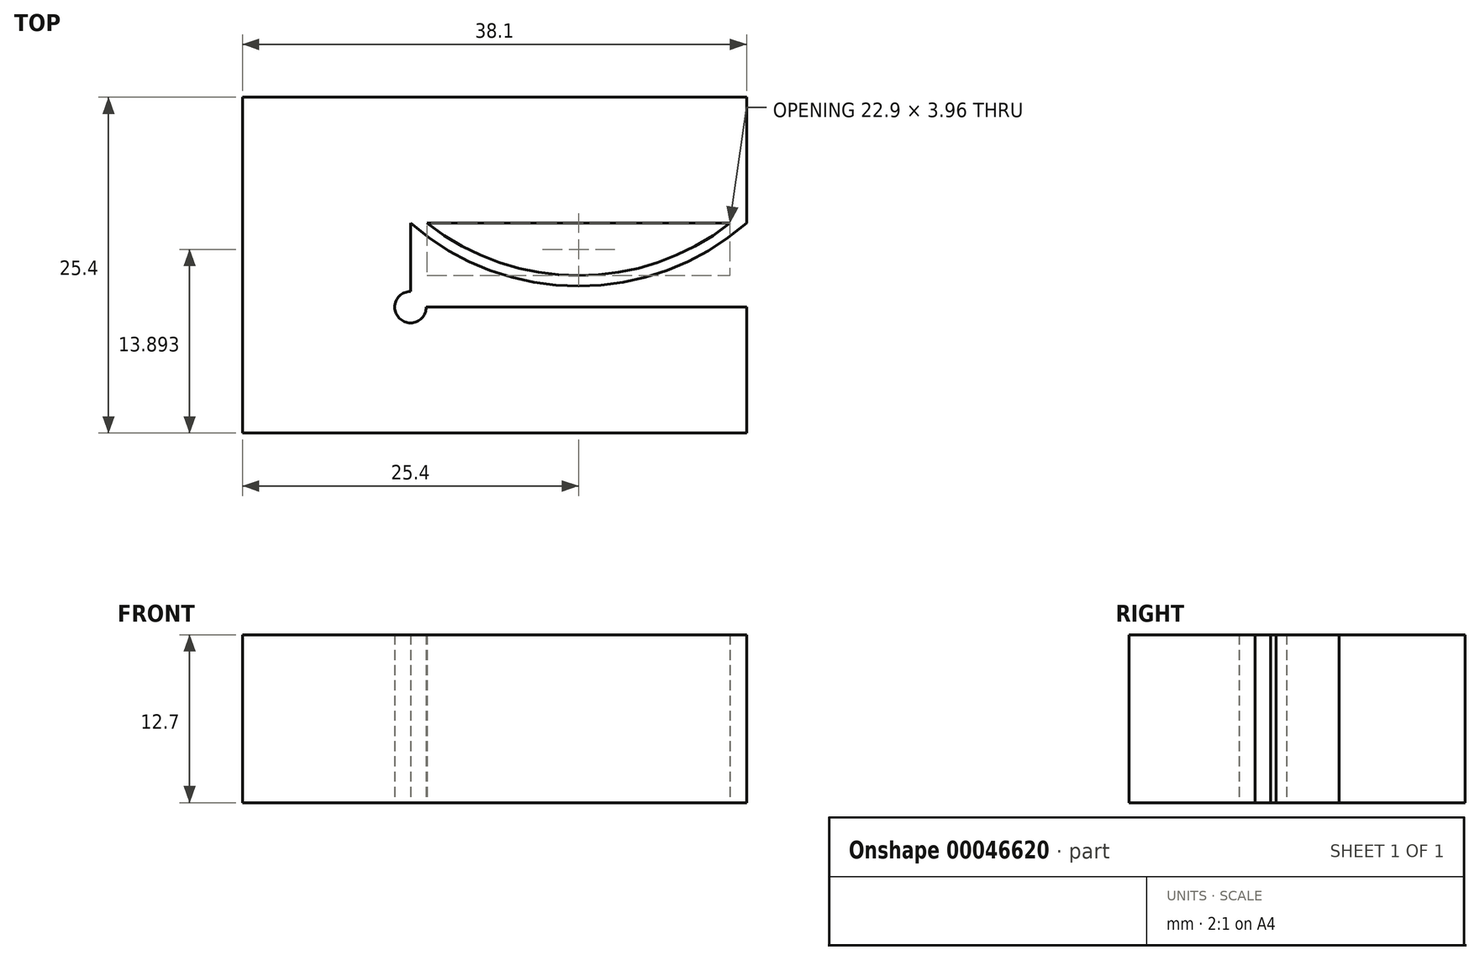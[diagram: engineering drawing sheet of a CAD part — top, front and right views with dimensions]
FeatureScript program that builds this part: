
annotation { "Feature Type Name" : "Feature", "Feature Type Description" : "" }
export const myFeature = defineFeature(function(context is Context, id is Id, definition is map)
    precondition{}
    {
        {
            var Q0;
            Q0=qCreatedBy(makeId("Top.planeOp"),FACE);
            var sketch = newSketch(context, id + "F0", { "sketchPlane" : qUnion([Q0])});
            skLineSegment(sketch, "E0.rect.bottom", {"start": v(-19.05, -12.7) * mm, "end": v(19.05, -12.7) * mm});
            skLineSegment(sketch, "E0.rect.top", {"start": v(-19.05, 12.7) * mm, "end": v(19.05, 12.7) * mm});
            skLineSegment(sketch, "E0.rect.left", {"start": v(-19.05, -12.7) * mm, "end": v(-19.05, 12.7) * mm});
            skLineSegment(sketch, "E0.rect.right", {"start": v(19.05, -12.7) * mm, "end": v(19.05, 12.7) * mm});
            skPoint(sketch, "E0.rect.middle", {"position": v(0, 0) * mm});
            skLineSegment(sketch, "E1.rect.bottom", {"start": v(-6.35, -3.18) * mm, "end": v(44.45, -3.18) * mm});
            skLineSegment(sketch, "E1.rect.top", {"start": v(-6.35, 3.17) * mm, "end": v(44.45, 3.17) * mm});
            skLineSegment(sketch, "E1.rect.left", {"start": v(-6.35, -3.18) * mm, "end": v(-6.35, 3.17) * mm});
            skLineSegment(sketch, "E1.rect.right", {"start": v(44.45, -3.18) * mm, "end": v(44.45, 3.17) * mm});
            skPoint(sketch, "E1.rect.middle", {"position": v(19.05, 0) * mm});
            skLineSegment(sketch, "E2", {"start": v(-6.35, -1.59) * mm, "end": v(19.05, -1.59) * mm, "construction": true});
            skCircle(sketch, "E3", {"center": v(6.35, 17.73) * mm, "radius": 19.31 * mm});
            skPoint(sketch, "E3.first.point", {"position": v(19.05, 3.17) * mm});
            skPoint(sketch, "E3.third.point", {"position": v(6.35, -1.59) * mm});
            skCircle(sketch, "E4", {"center": v(6.35, 17.73) * mm, "radius": 18.52 * mm});
            skCircle(sketch, "E5", {"center": v(-6.35, -3.18) * mm, "radius": 1.2 * mm});
            skSolve(sketch);
        }
        {
            var Q0;
            {var subQ11=sQuery(id+"F0.wireOp",EDGE,"E0.rect.bottom");Q0=makeQuery(id+"F0.imprint","IMPRINT",FACE,{"disambiguationData":[TD([[makeQuery(id+"F0.imprint","IMPRINT",EDGE,{"derivedFrom":subQ11}),1.0]])]});}
            var Q1;
            {var subQ3=sQuery(id+"F0.wireOp",EDGE,"E0.rect.top");var subQ5=sQuery(id+"F0.wireOp",EDGE,"E3");var subQ6=makeQuery(id+"F0.imprint","INTERSECT",VERTEX,{"derivedFrom":[subQ3,subQ5]});Q1=makeQuery(id+"F0.imprint","IMPRINT",FACE,{"disambiguationData":[TD([[makeQuery(id+"F0.imprint","IMPRINT",EDGE,{"disambiguationData":[TD([[subQ6,-1.0]])],"derivedFrom":subQ3}),-1.0]])]});}
            var Q2;
            {var subQ0=sQuery(id+"F0.wireOp",EDGE,"E0.rect.top");var subQ3=sQuery(id+"F0.wireOp",EDGE,"E0.rect.right");var subQ4=makeQuery(id+"F0.imprint","INTERSECT",VERTEX,{"derivedFrom":[subQ0,subQ3]});Q2=makeQuery(id+"F0.imprint","IMPRINT",FACE,{"disambiguationData":[TD([[makeQuery(id+"F0.imprint","IMPRINT",EDGE,{"disambiguationData":[TD([[subQ4,1.0]])],"derivedFrom":subQ0}),-1.0]])]});}
            var Q3;
            {var subQ0=sQuery(id+"F0.wireOp",EDGE,"E4");var subQ3=sQuery(id+"F0.wireOp",EDGE,"E0.rect.right");var subQ4=makeQuery(id+"F0.imprint","INTERSECT",VERTEX,{"derivedFrom":[subQ3,subQ0]});Q3=makeQuery(id+"F0.imprint","IMPRINT",FACE,{"disambiguationData":[TD([[makeQuery(id+"F0.imprint","IMPRINT",EDGE,{"disambiguationData":[TD([[subQ4,1.0]])],"derivedFrom":subQ0}),-1.0]])]});}
            var Q4;
            {var subQ0=sQuery(id+"F0.wireOp",EDGE,"E4");var subQ1=sQuery(id+"F0.wireOp",EDGE,"E1.rect.top");var subQ3=makeQuery(id+"F0.imprint","INTERSECT",VERTEX,{"disambiguationData":[OD(0.0)],"derivedFrom":[subQ1,subQ0]});Q4=makeQuery(id+"F0.imprint","IMPRINT",FACE,{"disambiguationData":[TD([[makeQuery(id+"F0.imprint","IMPRINT",EDGE,{"disambiguationData":[TD([[subQ3,-1.0]])],"derivedFrom":subQ0}),-1.0]])]});}
            extrude(context, id + "F1", {"entities" : qUnion([Q0, Q1, Q2, Q3, Q4]), "depth" : 12.7 * mm});
        }
    });
